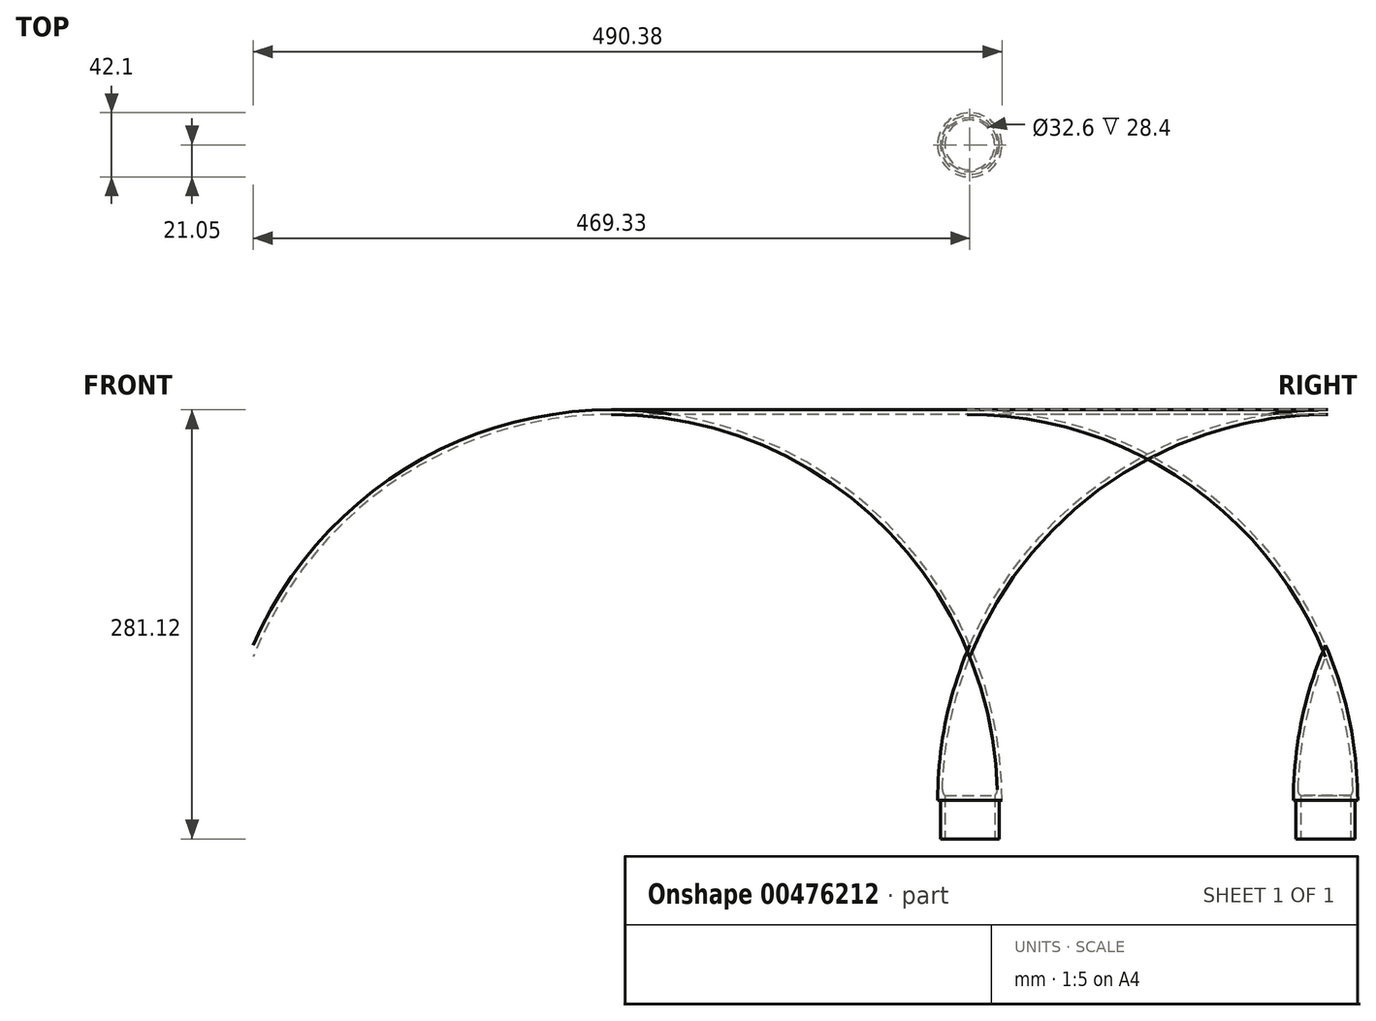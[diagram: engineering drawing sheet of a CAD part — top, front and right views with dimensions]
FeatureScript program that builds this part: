
annotation { "Feature Type Name" : "Feature", "Feature Type Description" : "" }
export const myFeature = defineFeature(function(context is Context, id is Id, definition is map)
    precondition{}
    {
        {
            var Q0;
            Q0=qCreatedBy(makeId("Front.planeOp"),FACE);
            var sketch = newSketch(context, id + "F0", { "sketchPlane" : qUnion([Q0])});
            skLineSegment(sketch, "E0", {"start": v(0, 0) * mm, "end": v(19.3, 0) * mm});
            skLineSegment(sketch, "E1", {"start": v(19.3, 0) * mm, "end": v(19.3, 25.4) * mm});
            skLineSegment(sketch, "E2", {"start": v(19.3, 25.4) * mm, "end": v(21.05, 25.4) * mm});
            skLineSegment(sketch, "E3", {"start": v(0, 0) * mm, "end": v(0, 127) * mm});
            skArc(sketch, "E4", {"start": v(21.05, 25.4) * mm, "mid": v(15.73, 77.28) * mm, "end": v(0, 127) * mm});
            skLineSegment(sketch, "E5", {"start": v(21.05, 25.4) * mm, "end": v(21.05, -4.81) * mm});
            skArc(sketch, "E6.0", {"start": v(18.03, 28.4) * mm, "mid": v(12.49, 78.14) * mm, "end": v(-2.75, 125.8) * mm});
            skLineSegment(sketch, "E6.1", {"start": v(16.3, 28.4) * mm, "end": v(18.03, 28.4) * mm});
            skLineSegment(sketch, "E6.2", {"start": v(16.3, 0) * mm, "end": v(16.3, 28.4) * mm});
            skSolve(sketch);
        }
        {
            var Q0;
            {var subQ4=sQuery(id+"F0.wireOp",EDGE,"E1");Q0=makeQuery(id+"F0.imprint","IMPRINT",FACE,{"disambiguationData":[TD([[makeQuery(id+"F0.imprint","IMPRINT",EDGE,{"derivedFrom":subQ4}),1.0]])]});}
            var Q1;
            Q1=sQuery(id+"F0.wireOp",EDGE,"E3");
            revolve(context, id + "F1", {"entities" : qUnion([Q0]), "axis" : qUnion([Q1]), "revolveType" : RevolveType.FULL});
        }
        {
            var Q0;
            Q0=makeQuery(id+"F1.opRevolve","SWEPT_EDGE",EDGE,{"disambiguationData":[OSD([sQuery(id+"F0.wireOp",EDGE,"E6.0"),sQuery(id+"F0.wireOp",EDGE,"E6.1")])]});
            fillet(context, id + "F2", {"entities" : qUnion([Q0]), "radius" : 5.08 * mm, "tangentPropagation" : true, "allowEdgeOverflow" : false});
        }
    });
